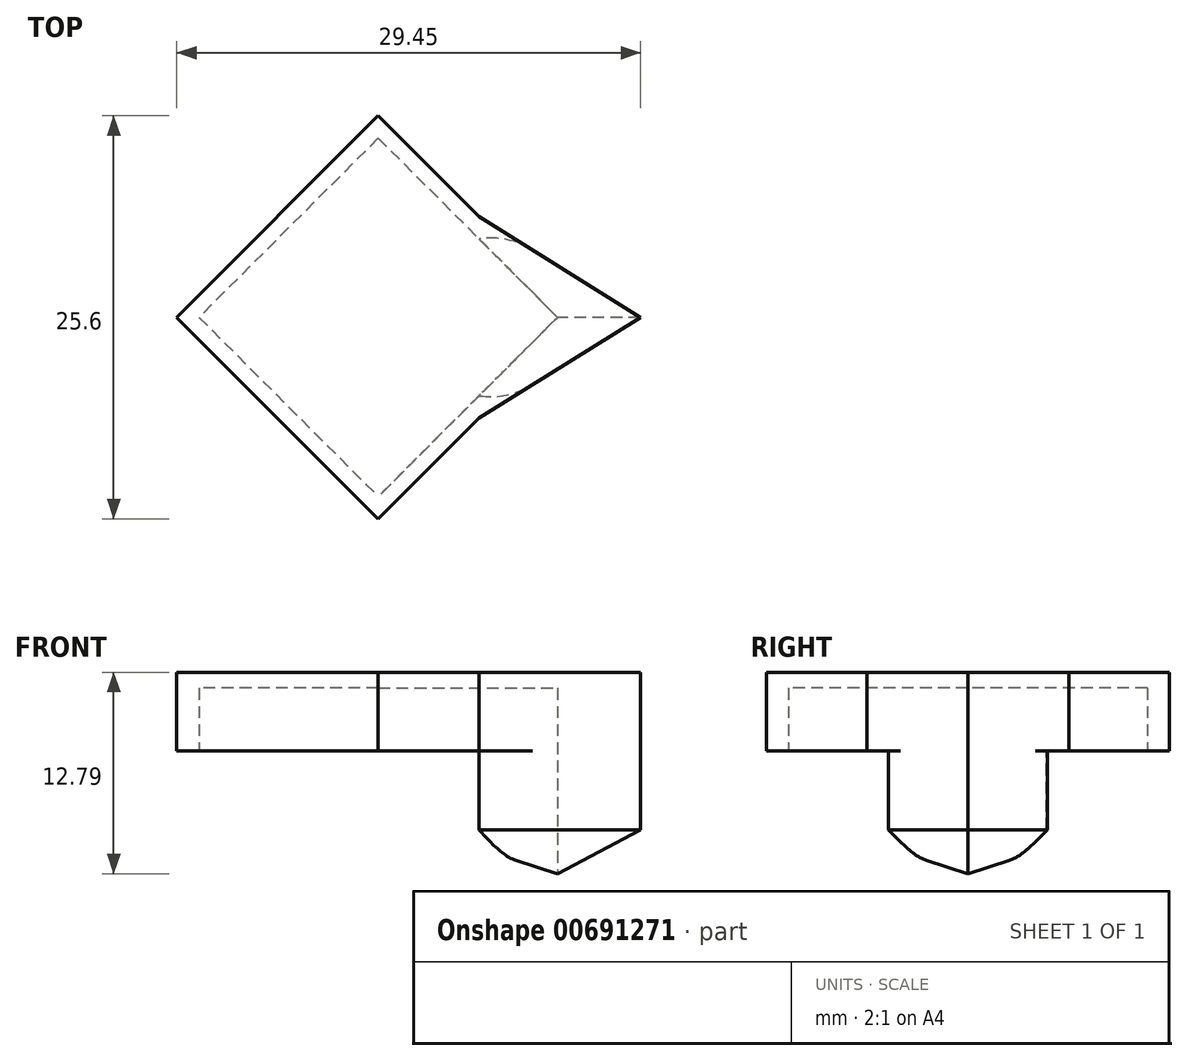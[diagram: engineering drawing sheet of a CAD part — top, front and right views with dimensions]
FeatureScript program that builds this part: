
annotation { "Feature Type Name" : "Feature", "Feature Type Description" : "" }
export const myFeature = defineFeature(function(context is Context, id is Id, definition is map)
    precondition{}
    {
        {
            var Q0;
            Q0=qCreatedBy(makeId("Right.planeOp"),FACE);
            var sketch = newSketch(context, id + "F0", { "sketchPlane" : qUnion([Q0])});
            skLineSegment(sketch, "E0", {"start": v(0, 0) * mm, "end": v(0, 47.78) * mm});
            skSolve(sketch);
        }
        {
            var Q0;
            Q0=qCreatedBy(makeId("Top.planeOp"),FACE);
            var sketch = newSketch(context, id + "F1", { "sketchPlane" : qUnion([Q0])});
            skLineSegment(sketch, "E1.bottom", {"start": v(-9.05, -9.05) * mm, "end": v(9.05, -9.05) * mm});
            skLineSegment(sketch, "E1.top", {"start": v(-9.05, 9.05) * mm, "end": v(9.05, 9.05) * mm});
            skLineSegment(sketch, "E1.left", {"start": v(-9.05, -9.05) * mm, "end": v(-9.05, 9.05) * mm});
            skLineSegment(sketch, "E1.right", {"start": v(9.05, -9.05) * mm, "end": v(9.05, 9.05) * mm});
            skPoint(sketch, "E1.middle", {"position": v(0, 0) * mm});
            skSolve(sketch);
        }
        {
            var Q0;
            Q0=makeQuery(id+"F1.imprint","IMPRINT",FACE,{"disambiguationData":[TD([[makeQuery(id+"F1.imprint","IMPRINT",EDGE,{"derivedFrom":sQuery(id+"F1.wireOp",EDGE,"E1.bottom")}),1.0]])]});
            extrude(context, id + "F2", {"entities" : qUnion([Q0]), "depth" : 5 * mm, "offsetDistance" : 25 * mm});
        }
        {
            var Q0;
            Q0=qCreatedBy(makeId("Top.planeOp"),FACE);
            var sketch = newSketch(context, id + "F3", { "sketchPlane" : qUnion([Q0])});
            skLineSegment(sketch, "E2.bottom", {"start": v(8.05, 8.05) * mm, "end": v(-8.05, 8.05) * mm});
            skLineSegment(sketch, "E2.top", {"start": v(8.05, -8.05) * mm, "end": v(-8.05, -8.05) * mm});
            skLineSegment(sketch, "E2.left", {"start": v(8.05, 8.05) * mm, "end": v(8.05, -8.05) * mm});
            skLineSegment(sketch, "E2.right", {"start": v(-8.05, 8.05) * mm, "end": v(-8.05, -8.05) * mm});
            skPoint(sketch, "E2.middle", {"position": v(0, 0) * mm});
            skSolve(sketch);
        }
        {
            var Q0;
            Q0=makeQuery(id+"F3.imprint","IMPRINT",FACE,{"disambiguationData":[TD([[makeQuery(id+"F3.imprint","IMPRINT",EDGE,{"derivedFrom":sQuery(id+"F3.wireOp",EDGE,"E2.bottom")}),1.0]])]});
            extrude(context, id + "F4", {"entities" : qUnion([Q0]), "operationType" : NewBodyOperationType.REMOVE, "depth" : 4 * mm, "offsetDistance" : 25 * mm});
        }
        {
            var Q0;
            Q0=makeQuery(id+"F2.opExtrude","SWEPT_BODY",BODY,{"disambiguationData":[OSD([sQuery(id+"F1.wireOp",EDGE,"E1.bottom"),sQuery(id+"F1.wireOp",EDGE,"E1.top"),sQuery(id+"F1.wireOp",EDGE,"E1.left"),sQuery(id+"F1.wireOp",EDGE,"E1.right")])]});
            var Q1;
            Q1=sQuery(id+"F0.wireOp",EDGE,"E0");
            transform(context, id + "F5", {"entities" : qUnion([Q0]), "transformType" : TransformType.ROTATION, "transformAxis" : qUnion([Q1]), "angle" : 45 * degree, "makeCopy" : false});
        }
        {
            var Q0;
            Q0=makeQuery(id+"F2.opExtrude","CAP_FACE",FACE,{"disambiguationData":[OSD([sQuery(id+"F1.wireOp",EDGE,"E1.bottom"),sQuery(id+"F1.wireOp",EDGE,"E1.top"),sQuery(id+"F1.wireOp",EDGE,"E1.left"),sQuery(id+"F1.wireOp",EDGE,"E1.right")])],"isStart":false});
            var sketch = newSketch(context, id + "F6", { "sketchPlane" : qUnion([Q0])});
            skLineSegment(sketch, "E3", {"start": v(6.4, -6.4) * mm, "end": v(16.65, 0) * mm});
            skLineSegment(sketch, "E4", {"start": v(16.65, 0) * mm, "end": v(6.4, 6.4) * mm});
            skSolve(sketch);
        }
        {
            var Q0;
            {var subQ0=sQuery(id+"F6.wireOp",EDGE,"E3");Q0=makeQuery(id+"F6.imprint","IMPRINT",FACE,{"disambiguationData":[TD([[makeQuery(id+"F6.imprint","IMPRINT",EDGE,{"derivedFrom":subQ0}),1.0]])]});}
            extrude(context, id + "F7", {"entities" : qUnion([Q0]), "operationType" : NewBodyOperationType.ADD, "oppositeDirection" : true, "depth" : 5 * mm, "offsetDistance" : 25 * mm});
        }
        {
            var Q0;
            {var subQ0=sQuery(id+"F1.wireOp",EDGE,"E1.right");var subQ1=sQuery(id+"F1.wireOp",EDGE,"E1.bottom");Q0=makeQuery(id+"F7.boolean.opBoolean","MERGE",FACE,{"derivedFrom":[makeQuery(id+"F2.opExtrude","CAP_FACE",FACE,{"disambiguationData":[OSD([subQ1,sQuery(id+"F1.wireOp",EDGE,"E1.top"),sQuery(id+"F1.wireOp",EDGE,"E1.left"),subQ0])],"isStart":true}),makeQuery(id+"F7.opExtrude","CAP_FACE",FACE,{"disambiguationData":[OSD([subQ1,subQ0,sQuery(id+"F6.wireOp",EDGE,"E3"),sQuery(id+"F6.wireOp",EDGE,"E4")])],"isStart":false})]});}
            var sketch = newSketch(context, id + "F8", { "sketchPlane" : qUnion([Q0])});
            skLineSegment(sketch, "E5", {"start": v(6.4, 6.4) * mm, "end": v(6.4, -6.4) * mm});
            skLineSegment(sketch, "E6", {"start": v(6.4, -6.4) * mm, "end": v(16.65, 0) * mm});
            skLineSegment(sketch, "E7", {"start": v(16.65, 0) * mm, "end": v(6.4, 6.4) * mm});
            skSolve(sketch);
        }
        {
            var Q0;
            {var subQ1=sQuery(id+"F8.wireOp",EDGE,"E6");Q0=makeQuery(id+"F8.imprint","IMPRINT",FACE,{"disambiguationData":[TD([[makeQuery(id+"F8.imprint","IMPRINT",EDGE,{"derivedFrom":subQ1}),-1.0]])]});}
            extrude(context, id + "F9", {"entities" : qUnion([Q0]), "operationType" : NewBodyOperationType.ADD, "depth" : 8 * mm, "offsetDistance" : 25 * mm});
        }
        {
            var Q0;
            Q0=makeQuery(id+"F9.opExtrude","SWEPT_EDGE",EDGE,{"disambiguationData":[OSD([sQuery(id+"F1.wireOp",EDGE,"E1.bottom"),sQuery(id+"F8.wireOp",EDGE,"E5"),sQuery(id+"F8.wireOp",EDGE,"E7")])]});
            var Q1;
            Q1=makeQuery(id+"F9.opExtrude","SWEPT_EDGE",EDGE,{"disambiguationData":[OSD([sQuery(id+"F1.wireOp",EDGE,"E1.right"),sQuery(id+"F8.wireOp",EDGE,"E5"),sQuery(id+"F8.wireOp",EDGE,"E6")])]});
            fillet(context, id + "F10", {"entities" : qUnion([Q0, Q1]), "radius" : 5 * mm, "tangentPropagation" : true, "allowEdgeOverflow" : false});
        }
        {
            var Q0;
            Q0=makeQuery(id+"F9.opExtrude","CAP_EDGE",EDGE,{"disambiguationData":[OSD([sQuery(id+"F8.wireOp",EDGE,"E6")])],"isStart":false});
            var Q1;
            Q1=makeQuery(id+"F9.opExtrude","CAP_EDGE",EDGE,{"disambiguationData":[OSD([sQuery(id+"F8.wireOp",EDGE,"E7")])],"isStart":false});
            chamfer(context, id + "F11", {"entities" : qUnion([Q0, Q1]), "width" : 3 * mm, "tangentPropagation" : true});
        }
    });
